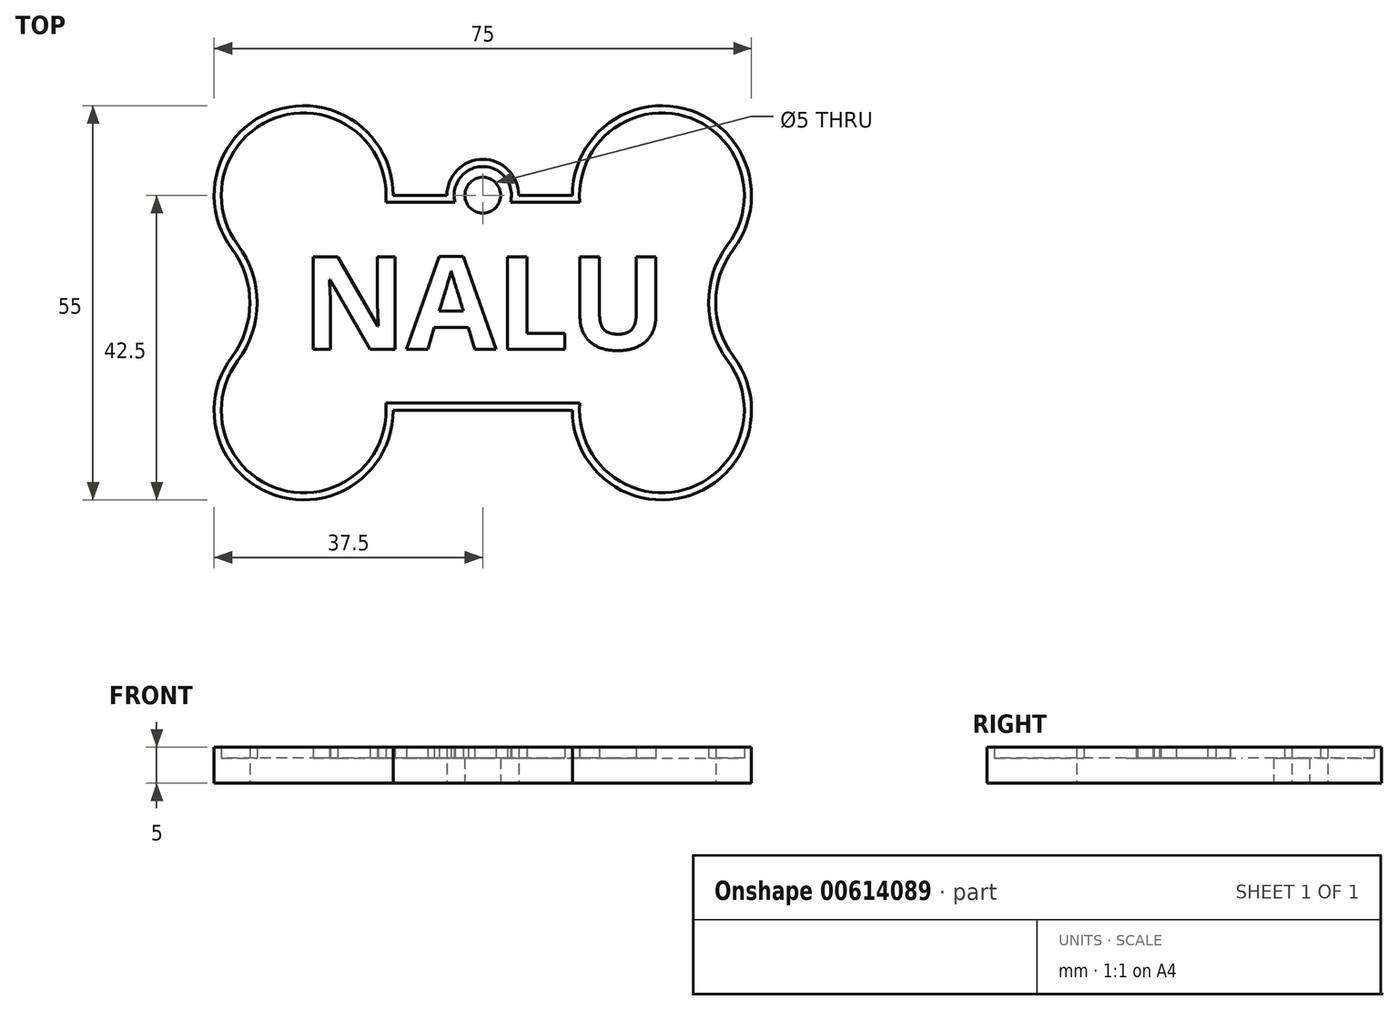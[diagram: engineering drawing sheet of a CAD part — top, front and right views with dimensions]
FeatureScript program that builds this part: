
annotation { "Feature Type Name" : "Feature", "Feature Type Description" : "" }
export const myFeature = defineFeature(function(context is Context, id is Id, definition is map)
    precondition{}
    {
        {
            var Q0;
            Q0=qCreatedBy(makeId("Top.planeOp"),FACE);
            var sketch = newSketch(context, id + "F0", { "sketchPlane" : qUnion([Q0])});
            skLineSegment(sketch, "E0", {"start": v(12.5, 0) * mm, "end": v(37.5, 0) * mm});
            skArc(sketch, "E1", {"start": v(12.5, 30) * mm, "mid": v(-3.95, 41.86) * mm, "end": v(-10, 22.5) * mm});
            skArc(sketch, "E2", {"start": v(60, 22.5) * mm, "mid": v(53.95, 41.86) * mm, "end": v(37.5, 30) * mm});
            skArc(sketch, "E3", {"start": v(-10, 7.5) * mm, "mid": v(-3.95, -11.86) * mm, "end": v(12.5, 0) * mm});
            skArc(sketch, "E4", {"start": v(37.5, 0) * mm, "mid": v(53.95, -11.86) * mm, "end": v(60, 7.5) * mm});
            skArc(sketch, "E5", {"start": v(-10, 7.5) * mm, "mid": v(-7.5, 15) * mm, "end": v(-10, 22.5) * mm});
            skPoint(sketch, "E5.first.point", {"position": v(-10, 22.5) * mm});
            skPoint(sketch, "E5.second.point", {"position": v(-10, 7.5) * mm});
            skPoint(sketch, "E5.third.point", {"position": v(-32.48, 15.7) * mm});
            skArc(sketch, "E6", {"start": v(60, 22.5) * mm, "mid": v(57.5, 15) * mm, "end": v(60, 7.5) * mm});
            skPoint(sketch, "E6.first.point", {"position": v(60, 22.5) * mm});
            skPoint(sketch, "E6.second.point", {"position": v(60, 7.5) * mm});
            skPoint(sketch, "E6.third.point", {"position": v(82.5, 14.76) * mm});
            skLineSegment(sketch, "E7.trimOffspring", {"start": v(37.5, 30) * mm, "end": v(30, 30) * mm});
            skLineSegment(sketch, "E8", {"start": v(12.5, 30) * mm, "end": v(20, 30) * mm, "construction": true});
            skCircle(sketch, "E9", {"center": v(25, 30) * mm, "radius": 2.5 * mm});
            skArc(sketch, "E10", {"start": v(30, 30) * mm, "mid": v(25, 35) * mm, "end": v(20, 30) * mm});
            skLineSegment(sketch, "E11.trimOffspring", {"start": v(20, 30) * mm, "end": v(12.5, 30) * mm});
            skSolve(sketch);
        }
        {
            var Q0;
            Q0 = qSketchRegion(id + "F0", true);
            extrude(context, id + "F1", {"entities" : qUnion([Q0]), "depth" : 3.5 * mm, "offsetDistance" : 25 * mm});
        }
        {
            var Q0;
            Q0=makeQuery(id+"F1.opExtrude","CAP_FACE",FACE,{"disambiguationData":[OSD([sQuery(id+"F0.wireOp",EDGE,"E0"),sQuery(id+"F0.wireOp",EDGE,"E1"),sQuery(id+"F0.wireOp",EDGE,"E2"),sQuery(id+"F0.wireOp",EDGE,"E3"),sQuery(id+"F0.wireOp",EDGE,"E4"),sQuery(id+"F0.wireOp",EDGE,"E5"),sQuery(id+"F0.wireOp",EDGE,"E6"),sQuery(id+"F0.wireOp",EDGE,"E7.trimOffspring"),sQuery(id+"F0.wireOp",EDGE,"E9"),sQuery(id+"F0.wireOp",EDGE,"E10"),sQuery(id+"F0.wireOp",EDGE,"E11.trimOffspring")])],"isStart":false});
            var sketch = newSketch(context, id + "F2", { "sketchPlane" : qUnion([Q0])});
            skText(sketch, "E12", { "text": "NALU", "fontName": "OpenSans-Bold.ttf"});
            skLineSegment(sketch, "E13.0", {"start": v(38.54, 29) * mm, "end": v(28.87, 29) * mm});
            skArc(sketch, "E13.1", {"start": v(59.2, 23.1) * mm, "mid": v(53.16, 41.06) * mm, "end": v(38.54, 29) * mm});
            skArc(sketch, "E13.2", {"start": v(28.87, 29) * mm, "mid": v(25, 34) * mm, "end": v(21.13, 29) * mm});
            skArc(sketch, "E13.3", {"start": v(59.2, 6.9) * mm, "mid": v(56.5, 15) * mm, "end": v(59.2, 23.1) * mm});
            skArc(sketch, "E13.4", {"start": v(38.54, 1) * mm, "mid": v(53.16, -11.06) * mm, "end": v(59.2, 6.9) * mm});
            skLineSegment(sketch, "E13.5", {"start": v(11.46, 1) * mm, "end": v(38.54, 1) * mm});
            skLineSegment(sketch, "E13.6", {"start": v(21.13, 29) * mm, "end": v(11.46, 29) * mm});
            skArc(sketch, "E13.7", {"start": v(11.46, 29) * mm, "mid": v(-3.16, 41.06) * mm, "end": v(-9.2, 23.1) * mm});
            skArc(sketch, "E13.8", {"start": v(-9.2, 23.1) * mm, "mid": v(-6.5, 15) * mm, "end": v(-9.2, 6.9) * mm});
            skArc(sketch, "E13.9", {"start": v(-9.2, 6.9) * mm, "mid": v(-3.16, -11.06) * mm, "end": v(11.46, 1) * mm});
            const initialGuessF2  = {"E12": [-0.00031, 0.0085, 1, 0, 0.013]};
            skSetInitialGuess(sketch, initialGuessF2);
            skSolve(sketch);
        }
        {
            var Q0;
            Q0=makeQuery(id+"F2.imprint","IMPRINT",FACE,{"disambiguationData":[TD([[makeQuery(id+"F2.imprint","IMPRINT",EDGE,{"derivedFrom":sQuery(id+"F2.wireOp",EDGE,"E13.0")}),-1.0]])]});
            var Q1;
            Q1=makeQuery(id+"F2.imprint","IMPRINT",FACE,{"disambiguationData":[TD([[makeQuery(id+"F2.imprint","IMPRINT",EDGE,{"derivedFrom":sQuery(id+"F2.wireOp",EDGE,"E12.sketch_text.stroke-0")}),-1.0]])]});
            var Q2;
            Q2=makeQuery(id+"F2.imprint","IMPRINT",FACE,{"disambiguationData":[TD([[makeQuery(id+"F2.imprint","IMPRINT",EDGE,{"derivedFrom":sQuery(id+"F2.wireOp",EDGE,"E12.sketch_text.stroke-14")}),-1.0]])]});
            var Q3;
            Q3=makeQuery(id+"F2.imprint","IMPRINT",FACE,{"disambiguationData":[TD([[makeQuery(id+"F2.imprint","IMPRINT",EDGE,{"derivedFrom":sQuery(id+"F2.wireOp",EDGE,"E12.sketch_text.stroke-26")}),-1.0]])]});
            var Q4;
            Q4=makeQuery(id+"F2.imprint","IMPRINT",FACE,{"disambiguationData":[TD([[makeQuery(id+"F2.imprint","IMPRINT",EDGE,{"derivedFrom":sQuery(id+"F2.wireOp",EDGE,"E12.sketch_text.stroke-32")}),-1.0]])]});
            extrude(context, id + "F3", {"entities" : qUnion([Q0, Q1, Q2, Q3, Q4]), "operationType" : NewBodyOperationType.ADD, "depth" : 1.5 * mm, "offsetDistance" : 25 * mm});
        }
    });
